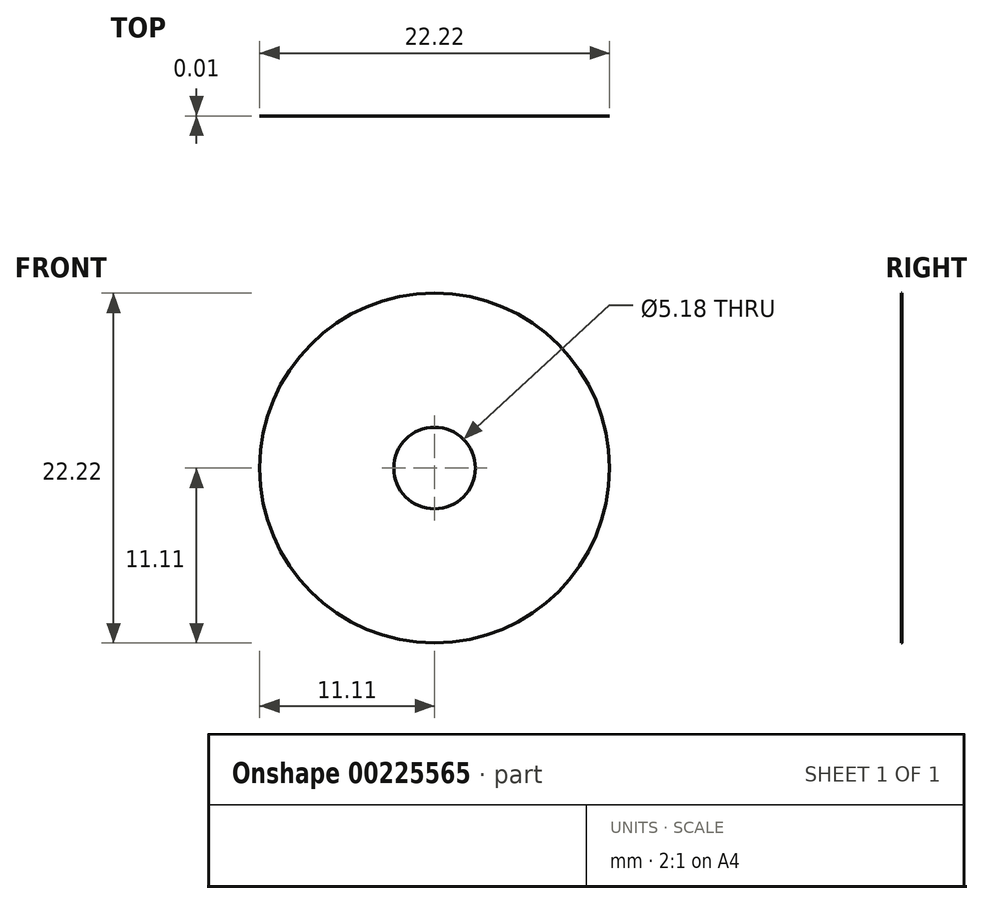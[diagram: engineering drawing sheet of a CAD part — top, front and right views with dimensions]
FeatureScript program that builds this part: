
annotation { "Feature Type Name" : "Feature", "Feature Type Description" : "" }
export const myFeature = defineFeature(function(context is Context, id is Id, definition is map)
    precondition{}
    {
        {
            var Q0;
            Q0=qCreatedBy(makeId("Front.planeOp"),FACE);
            var sketch = newSketch(context, id + "F0", { "sketchPlane" : qUnion([Q0])});
            skCircle(sketch, "E0", {"center": v(0, 0) * mm, "radius": 11.11 * mm});
            skSolve(sketch);
        }
        {
            var Q0;
            Q0 = qSketchRegion(id + "F0", true);
            extrude(context, id + "F1", {"entities" : qUnion([Q0]), "depth" : 2 / 203.2 * mm});
        }
        {
            var Q0;
            Q0=makeQuery(id+"F1.opExtrude","CAP_FACE",FACE,{"disambiguationData":[OSD([sQuery(id+"F0.wireOp",EDGE,"E0")])],"isStart":false});
            var sketch = newSketch(context, id + "F2", { "sketchPlane" : qUnion([Q0])});
            skPoint(sketch, "E1", {"position": v(0, 0) * mm});
            skSolve(sketch);
        }
        {
            var Q0;
            Q0=sQuery(id+"F2.wireOp",VERTEX,"E1");
            var Q1;
            Q1=makeQuery(id+"F1.opExtrude","SWEPT_BODY",BODY,{"disambiguationData":[OSD([sQuery(id+"F0.wireOp",EDGE,"E0")])]});
            hole(context, id + "F3", {"style" : HoleStyle.SIMPLE, "endStyle" : HoleEndStyle.THROUGH, "holeDiameter" : 5.18 * mm, "locations" : qUnion([Q0]), "scope" : qUnion([Q1]), "isTappedThrough" : true});
        }
    });
